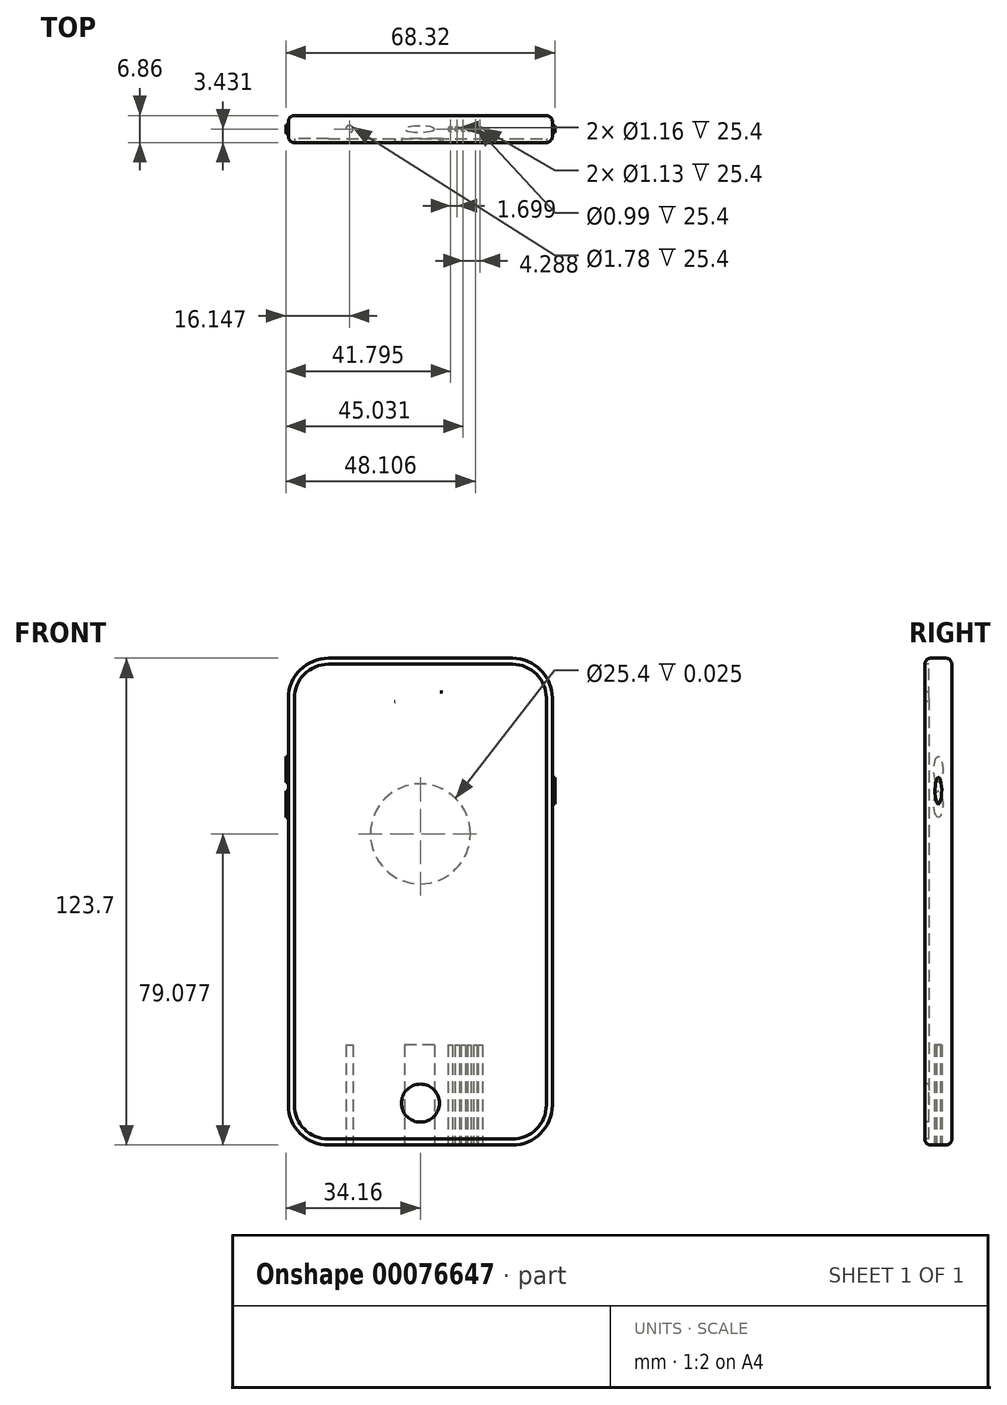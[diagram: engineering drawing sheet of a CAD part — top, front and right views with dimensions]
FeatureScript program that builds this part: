
annotation { "Feature Type Name" : "Feature", "Feature Type Description" : "" }
export const myFeature = defineFeature(function(context is Context, id is Id, definition is map)
    precondition{}
    {
        {
            var Q0;
            Q0=qCreatedBy(makeId("Front.planeOp"),FACE);
            var sketch = newSketch(context, id + "F0", { "sketchPlane" : qUnion([Q0])});
            skLineSegment(sketch, "E0.bottom", {"start": v(-33.33, 66.72) * mm, "end": v(33.73, 66.72) * mm});
            skLineSegment(sketch, "E0.top", {"start": v(-33.33, -56.98) * mm, "end": v(33.73, -56.98) * mm});
            skLineSegment(sketch, "E0.left", {"start": v(-33.33, 66.72) * mm, "end": v(-33.33, -56.98) * mm});
            skLineSegment(sketch, "E0.right", {"start": v(33.73, 66.72) * mm, "end": v(33.73, -56.98) * mm});
            skSolve(sketch);
        }
        {
            var Q0;
            Q0=qSketchRegion(id+"F0",true);
            extrude(context, id + "F1", {"entities" : qUnion([Q0]), "depth" : 6.86 * mm});
        }
        {
            var Q0;
            Q0=makeQuery(id+"F1.opExtrude","SWEPT_EDGE",EDGE,{"disambiguationData":[OSD([sQuery(id+"F0.wireOp",EDGE,"E0.bottom"),sQuery(id+"F0.wireOp",EDGE,"E0.left")])]});
            var Q1;
            Q1=makeQuery(id+"F1.opExtrude","SWEPT_EDGE",EDGE,{"disambiguationData":[OSD([sQuery(id+"F0.wireOp",EDGE,"E0.bottom"),sQuery(id+"F0.wireOp",EDGE,"E0.right")])]});
            fillet(context, id + "F2", {"entities" : qUnion([Q0, Q1]), "radius" : 10.16 * mm, "tangentPropagation" : true, "allowEdgeOverflow" : false});
        }
        {
            var Q0;
            Q0=makeQuery(id+"F1.opExtrude","SWEPT_EDGE",EDGE,{"disambiguationData":[OSD([sQuery(id+"F0.wireOp",EDGE,"E0.top"),sQuery(id+"F0.wireOp",EDGE,"E0.left")])]});
            var Q1;
            Q1=makeQuery(id+"F1.opExtrude","SWEPT_EDGE",EDGE,{"disambiguationData":[OSD([sQuery(id+"F0.wireOp",EDGE,"E0.top"),sQuery(id+"F0.wireOp",EDGE,"E0.right")])]});
            fillet(context, id + "F3", {"entities" : qUnion([Q0, Q1]), "radius" : 10.16 * mm, "tangentPropagation" : true, "allowEdgeOverflow" : false});
        }
        {
            var Q0;
            Q0=makeQuery(id+"F1.opExtrude","CAP_EDGE",EDGE,{"disambiguationData":[OSD([sQuery(id+"F0.wireOp",EDGE,"E0.right")])],"isStart":true});
            fillet(context, id + "F4", {"entities" : qUnion([Q0]), "radius" : 1.52 * mm, "tangentPropagation" : true, "allowEdgeOverflow" : false});
        }
        {
            var Q0;
            Q0=makeQuery(id+"F1.opExtrude","CAP_EDGE",EDGE,{"disambiguationData":[OSD([sQuery(id+"F0.wireOp",EDGE,"E0.right")])],"isStart":false});
            fillet(context, id + "F5", {"entities" : qUnion([Q0]), "radius" : 1.52 * mm, "tangentPropagation" : true, "allowEdgeOverflow" : false});
        }
        {
            var Q0;
            Q0=makeQuery(id+"F1.opExtrude","CAP_FACE",FACE,{"disambiguationData":[OSD([sQuery(id+"F0.wireOp",EDGE,"E0.bottom"),sQuery(id+"F0.wireOp",EDGE,"E0.top"),sQuery(id+"F0.wireOp",EDGE,"E0.left"),sQuery(id+"F0.wireOp",EDGE,"E0.right")])],"isStart":false});
            var sketch = newSketch(context, id + "F6", { "sketchPlane" : qUnion([Q0])});
            skLineSegment(sketch, "E1.0", {"start": v(30.68, 48.43) * mm, "end": v(-30.28, 48.43) * mm});
            skLineSegment(sketch, "E2.0", {"start": v(-30.28, -38.7) * mm, "end": v(30.68, -38.7) * mm});
            skLineSegment(sketch, "E3.0", {"start": v(-30.28, 48.43) * mm, "end": v(-30.28, -38.7) * mm});
            skLineSegment(sketch, "E4.0", {"start": v(30.68, -38.7) * mm, "end": v(30.68, 48.43) * mm});
            skCircle(sketch, "E5", {"center": v(0.2, -46.31) * mm, "radius": 5.46 * mm});
            skLineSegment(sketch, "E6.0", {"start": v(23.57, 56.81) * mm, "end": v(6.78, 56.81) * mm});
            skCircle(sketch, "E7", {"center": v(-15.3, 56.81) * mm, "radius": 2.54 * mm});
            skCircle(sketch, "E8", {"center": v(0, 61.1) * mm, "radius": 1.12 * mm});
            skLineSegment(sketch, "E9", {"start": v(-6.37, 55.68) * mm, "end": v(5.57, 55.68) * mm});
            skLineSegment(sketch, "E10", {"start": v(5.86, 58.11) * mm, "end": v(-6.43, 58.11) * mm});
            skArc(sketch, "E11", {"start": v(-6.14, 58.11) * mm, "mid": v(-7.5, 56.93) * mm, "end": v(-6.2, 55.68) * mm});
            skArc(sketch, "E12", {"start": v(5.53, 55.68) * mm, "mid": v(6.77, 57.07) * mm, "end": v(5.23, 58.11) * mm});
            skPoint(sketch, "E13.orphan", {"position": v(-10.28, 58.11) * mm});
            skPoint(sketch, "E14.end.orphan", {"position": v(9.44, 58.11) * mm});
            skLineSegment(sketch, "E15.trimOffspring", {"start": v(-7.5, 56.81) * mm, "end": v(-23.17, 56.81) * mm});
            skCircle(sketch, "E16", {"center": v(0.2, -46.31) * mm, "radius": 4.82 * mm});
            skSolve(sketch);
        }
        {
            var Q0;
            Q0=makeQuery(id+"F6.imprint","IMPRINT",FACE,{"disambiguationData":[TD([[makeQuery(id+"F6.imprint","IMPRINT",EDGE,{"derivedFrom":sQuery(id+"F6.wireOp",EDGE,"E8")}),1.0]])]});
            var Q1;
            Q1=makeQuery(id+"F6.imprint","IMPRINT",FACE,{"disambiguationData":[TD([[makeQuery(id+"F6.imprint","IMPRINT",EDGE,{"derivedFrom":sQuery(id+"F6.wireOp",EDGE,"E5")}),1.0]])]});
            var Q2;
            {var subQ0=sQuery(id+"F6.wireOp",EDGE,"E15.trimOffspring");var subQ1=sQuery(id+"F6.wireOp",EDGE,"E7");var subQ3=makeQuery(id+"F6.imprint","INTERSECT",VERTEX,{"disambiguationData":[OD(0.0)],"derivedFrom":[subQ1,subQ0]});Q2=makeQuery(id+"F6.imprint","IMPRINT",FACE,{"disambiguationData":[TD([[makeQuery(id+"F6.imprint","IMPRINT",EDGE,{"disambiguationData":[TD([[subQ3,1.0]])],"derivedFrom":subQ1}),1.0]])]});}
            var Q3;
            {var subQ0=sQuery(id+"F6.wireOp",EDGE,"E15.trimOffspring");var subQ1=sQuery(id+"F6.wireOp",EDGE,"E7");var subQ3=makeQuery(id+"F6.imprint","INTERSECT",VERTEX,{"disambiguationData":[OD(0.0)],"derivedFrom":[subQ1,subQ0]});Q3=makeQuery(id+"F6.imprint","IMPRINT",FACE,{"disambiguationData":[TD([[makeQuery(id+"F6.imprint","IMPRINT",EDGE,{"disambiguationData":[TD([[subQ3,-1.0]])],"derivedFrom":subQ1}),1.0]])]});}
            var Q4;
            {var subQ0=sQuery(id+"F6.wireOp",EDGE,"E11");var subQ1=sQuery(id+"F6.wireOp",EDGE,"E9");var subQ3=makeQuery(id+"F6.imprint","INTERSECT",VERTEX,{"disambiguationData":[OD(0.0)],"derivedFrom":[subQ1,subQ0]});Q4=makeQuery(id+"F6.imprint","IMPRINT",FACE,{"disambiguationData":[TD([[makeQuery(id+"F6.imprint","IMPRINT",EDGE,{"disambiguationData":[TD([[subQ3,-1.0]])],"derivedFrom":subQ1}),-1.0]])]});}
            var Q5;
            {var subQ0=sQuery(id+"F6.wireOp",EDGE,"E12");var subQ1=sQuery(id+"F6.wireOp",EDGE,"E9");var subQ3=makeQuery(id+"F6.imprint","INTERSECT",VERTEX,{"disambiguationData":[OD(0.0)],"derivedFrom":[subQ1,subQ0]});Q5=makeQuery(id+"F6.imprint","IMPRINT",FACE,{"disambiguationData":[TD([[makeQuery(id+"F6.imprint","IMPRINT",EDGE,{"disambiguationData":[TD([[subQ3,1.0]])],"derivedFrom":subQ1}),-1.0]])]});}
            var Q6;
            {var subQ0=sQuery(id+"F6.wireOp",EDGE,"E12");var subQ1=sQuery(id+"F6.wireOp",EDGE,"E10");var subQ3=makeQuery(id+"F6.imprint","INTERSECT",VERTEX,{"disambiguationData":[OD(0.0)],"derivedFrom":[subQ1,subQ0]});Q6=makeQuery(id+"F6.imprint","IMPRINT",FACE,{"disambiguationData":[TD([[makeQuery(id+"F6.imprint","IMPRINT",EDGE,{"disambiguationData":[TD([[subQ3,-1.0]])],"derivedFrom":subQ1}),-1.0]])]});}
            var Q7;
            {var subQ0=sQuery(id+"F6.wireOp",EDGE,"E11");var subQ1=sQuery(id+"F6.wireOp",EDGE,"E10");var subQ3=makeQuery(id+"F6.imprint","INTERSECT",VERTEX,{"disambiguationData":[OD(0.0)],"derivedFrom":[subQ1,subQ0]});Q7=makeQuery(id+"F6.imprint","IMPRINT",FACE,{"disambiguationData":[TD([[makeQuery(id+"F6.imprint","IMPRINT",EDGE,{"disambiguationData":[TD([[subQ3,1.0]])],"derivedFrom":subQ1}),-1.0]])]});}
            var Q8;
            {var subQ0=sQuery(id+"F6.wireOp",EDGE,"E11");var subQ1=makeQuery(id+"F6.imprint","IMPRINT",VERTEX,{"derivedFrom":subQ0});Q8=makeQuery(id+"F6.imprint","IMPRINT",FACE,{"disambiguationData":[TD([[makeQuery(id+"F6.imprint","IMPRINT",EDGE,{"disambiguationData":[TD([[subQ1,1.0]])],"derivedFrom":subQ0}),1.0]])]});}
            var Q9;
            Q9=makeQuery(id+"F6.imprint","IMPRINT",FACE,{"disambiguationData":[TD([[makeQuery(id+"F6.imprint","IMPRINT",EDGE,{"derivedFrom":sQuery(id+"F6.wireOp",EDGE,"E1.0")}),1.0]])]});
            extrude(context, id + "F7", {"entities" : qUnion([Q0, Q1, Q2, Q3, Q4, Q5, Q6, Q7, Q8, Q9]), "operationType" : NewBodyOperationType.REMOVE, "oppositeDirection" : true, "depth" : 1.02 * mm});
        }
        {
            var Q0;
            Q0=makeQuery(id+"F1.opExtrude","SWEPT_FACE",FACE,{"disambiguationData":[OSD([sQuery(id+"F0.wireOp",EDGE,"E0.top")])]});
            var sketch = newSketch(context, id + "F8", { "sketchPlane" : qUnion([Q0])});
            skLineSegment(sketch, "E17", {"start": v(-23.17, 5.33) * mm, "end": v(-23.17, 1.52) * mm});
            skCircle(sketch, "E18", {"center": v(-17.81, 3.43) * mm, "radius": 0.9 * mm});
            skLineSegment(sketch, "E19", {"start": v(-23.17, 5.33) * mm, "end": v(23.57, 5.33) * mm});
            skEllipse(sketch, "E20", {"center": v(0, 3.43) * mm, "majorRadius": 3.79 * mm, "minorRadius": 0.94 * mm, "majorAxis": v(1, 0)});
            skCircle(sketch, "E21", {"center": v(7.83, 3.43) * mm, "radius": 0.58 * mm});
            skCircle(sketch, "E22", {"center": v(9.53, 3.43) * mm, "radius": 0.58 * mm});
            skCircle(sketch, "E23", {"center": v(11.07, 3.43) * mm, "radius": 0.56 * mm});
            skCircle(sketch, "E24", {"center": v(12.6, 3.43) * mm, "radius": 0.49 * mm});
            skCircle(sketch, "E25", {"center": v(14.15, 3.43) * mm, "radius": 0.5 * mm});
            skCircle(sketch, "E26", {"center": v(15.36, 3.43) * mm, "radius": 0.56 * mm});
            skSolve(sketch);
        }
        {
            var Q0;
            Q0=makeQuery(id+"F8.imprint","IMPRINT",FACE,{"disambiguationData":[TD([[makeQuery(id+"F8.imprint","IMPRINT",EDGE,{"derivedFrom":sQuery(id+"F8.wireOp",EDGE,"E18")}),1.0]])]});
            var Q1;
            Q1=makeQuery(id+"F8.imprint","IMPRINT",FACE,{"disambiguationData":[TD([[makeQuery(id+"F8.imprint","IMPRINT",EDGE,{"derivedFrom":sQuery(id+"F8.wireOp",EDGE,"E20")}),1.0]])]});
            var Q2;
            Q2=makeQuery(id+"F8.imprint","IMPRINT",FACE,{"disambiguationData":[TD([[makeQuery(id+"F8.imprint","IMPRINT",EDGE,{"derivedFrom":sQuery(id+"F8.wireOp",EDGE,"E22")}),1.0]])]});
            var Q3;
            Q3=makeQuery(id+"F8.imprint","IMPRINT",FACE,{"disambiguationData":[TD([[makeQuery(id+"F8.imprint","IMPRINT",EDGE,{"derivedFrom":sQuery(id+"F8.wireOp",EDGE,"E23")}),1.0]])]});
            var Q4;
            Q4=makeQuery(id+"F8.imprint","IMPRINT",FACE,{"disambiguationData":[TD([[makeQuery(id+"F8.imprint","IMPRINT",EDGE,{"derivedFrom":sQuery(id+"F8.wireOp",EDGE,"E24")}),1.0]])]});
            var Q5;
            Q5=makeQuery(id+"F8.imprint","IMPRINT",FACE,{"disambiguationData":[TD([[makeQuery(id+"F8.imprint","IMPRINT",EDGE,{"derivedFrom":sQuery(id+"F8.wireOp",EDGE,"E25")}),1.0]])]});
            var Q6;
            Q6=makeQuery(id+"F8.imprint","IMPRINT",FACE,{"disambiguationData":[TD([[makeQuery(id+"F8.imprint","IMPRINT",EDGE,{"derivedFrom":sQuery(id+"F8.wireOp",EDGE,"E26")}),1.0]])]});
            var Q7;
            Q7=makeQuery(id+"F8.imprint","IMPRINT",FACE,{"disambiguationData":[TD([[makeQuery(id+"F8.imprint","IMPRINT",EDGE,{"derivedFrom":sQuery(id+"F8.wireOp",EDGE,"E21")}),1.0]])]});
            extrude(context, id + "F9", {"entities" : qUnion([Q0, Q1, Q2, Q3, Q4, Q5, Q6, Q7]), "operationType" : NewBodyOperationType.REMOVE, "oppositeDirection" : true, "depth" : 25.4 * mm});
        }
        {
            var Q0;
            Q0=makeQuery(id+"F1.opExtrude","SWEPT_FACE",FACE,{"disambiguationData":[OSD([sQuery(id+"F0.wireOp",EDGE,"E0.right")])]});
            var sketch = newSketch(context, id + "F10", { "sketchPlane" : qUnion([Q0])});
            skEllipse(sketch, "E27", {"center": v(-3.43, 33.07) * mm, "majorRadius": 3.36 * mm, "minorRadius": 0.85 * mm, "majorAxis": v(0, -1)});
            skSolve(sketch);
        }
        {
            var Q0;
            Q0=makeQuery(id+"F10.imprint","IMPRINT",FACE,{"disambiguationData":[TD([[makeQuery(id+"F10.imprint","IMPRINT",EDGE,{"derivedFrom":sQuery(id+"F10.wireOp",EDGE,"E27")}),1.0]])]});
            extrude(context, id + "F11", {"entities" : qUnion([Q0]), "operationType" : NewBodyOperationType.ADD, "depth" : 0.64 * mm});
        }
        {
            var Q0;
            Q0=makeQuery(id+"F1.opExtrude","SWEPT_FACE",FACE,{"disambiguationData":[OSD([sQuery(id+"F0.wireOp",EDGE,"E0.left")])]});
            var sketch = newSketch(context, id + "F12", { "sketchPlane" : qUnion([Q0])});
            skEllipse(sketch, "E28", {"center": v(3.43, 38.42) * mm, "majorRadius": 3.32 * mm, "minorRadius": 1.12 * mm, "majorAxis": v(0, -1)});
            skEllipse(sketch, "E29", {"center": v(3.43, 29.66) * mm, "majorRadius": 3.35 * mm, "minorRadius": 1.12 * mm, "majorAxis": v(0, -1)});
            skSolve(sketch);
        }
        {
            var Q0;
            Q0=qSketchRegion(id+"F12",true);
            extrude(context, id + "F13", {"entities" : qUnion([Q0]), "operationType" : NewBodyOperationType.ADD, "depth" : 0.64 * mm});
        }
        {
            var Q0;
            Q0=makeQuery(id+"F1.opExtrude","CAP_FACE",FACE,{"disambiguationData":[OSD([sQuery(id+"F0.wireOp",EDGE,"E0.bottom"),sQuery(id+"F0.wireOp",EDGE,"E0.top"),sQuery(id+"F0.wireOp",EDGE,"E0.left"),sQuery(id+"F0.wireOp",EDGE,"E0.right")])],"isStart":true});
            var sketch = newSketch(context, id + "F14", { "sketchPlane" : qUnion([Q0])});
            skCircle(sketch, "E30", {"center": v(-0.2, 22.1) * mm, "radius": 12.7 * mm});
            skSolve(sketch);
        }
        {
            var Q0;
            Q0=makeQuery(id+"F14.imprint","IMPRINT",FACE,{"disambiguationData":[TD([[makeQuery(id+"F14.imprint","IMPRINT",EDGE,{"derivedFrom":sQuery(id+"F14.wireOp",EDGE,"E30")}),1.0]])]});
            extrude(context, id + "F15", {"entities" : qUnion([Q0]), "operationType" : NewBodyOperationType.REMOVE, "oppositeDirection" : true, "depth" : 0.03 * mm});
        }
    });
